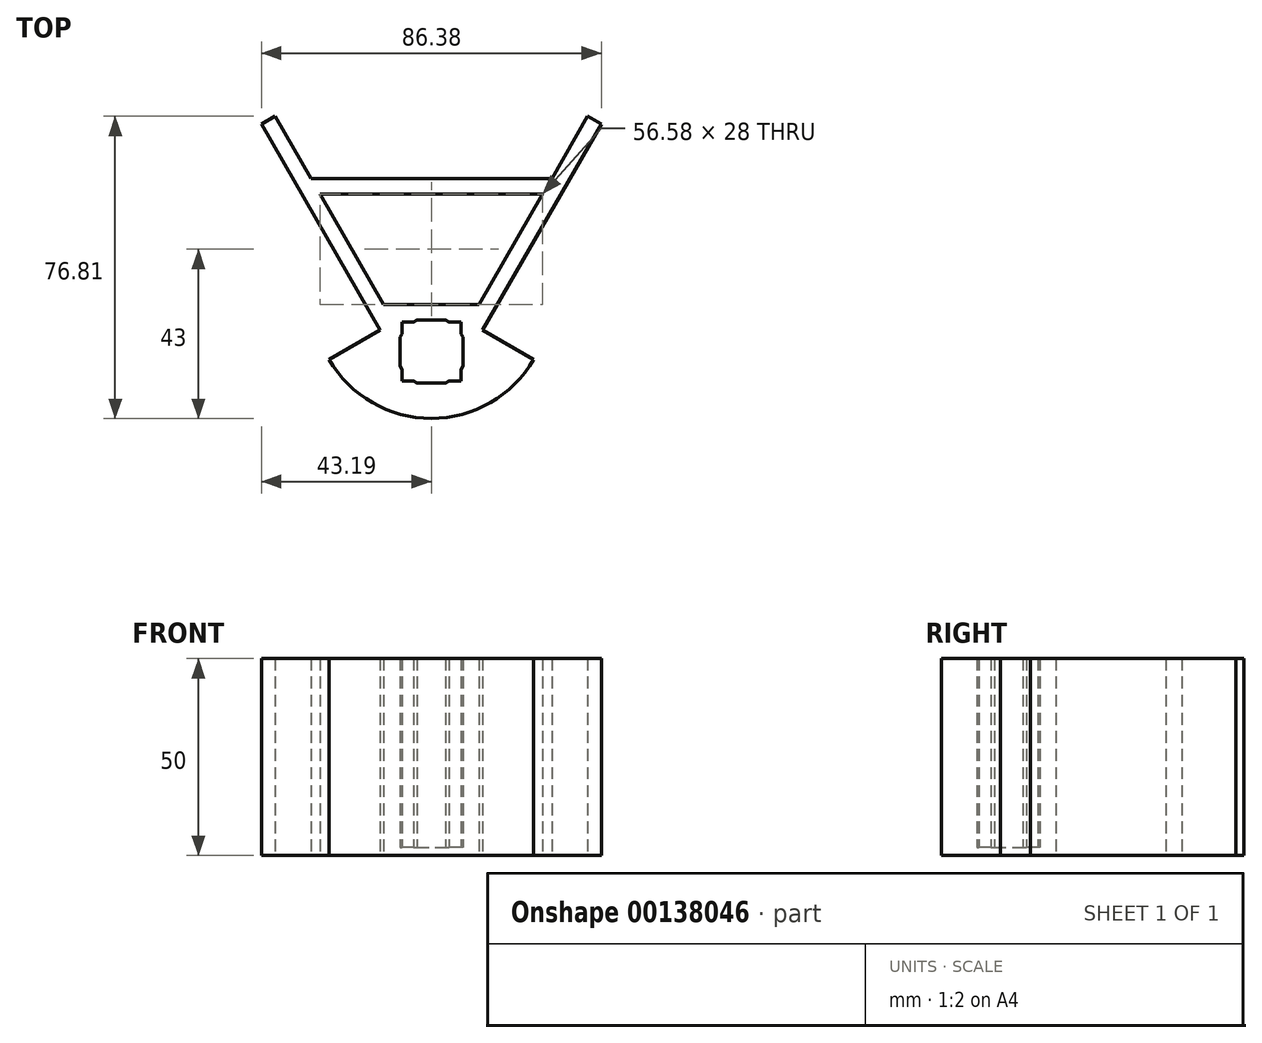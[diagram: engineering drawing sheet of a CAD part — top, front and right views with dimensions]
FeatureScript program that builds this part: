
annotation { "Feature Type Name" : "Feature", "Feature Type Description" : "" }
export const myFeature = defineFeature(function(context is Context, id is Id, definition is map)
    precondition{}
    {
        {
            var Q0;
            Q0=qCreatedBy(makeId("Top.planeOp"),FACE);
            var sketch = newSketch(context, id + "F0", { "sketchPlane" : qUnion([Q0])});
            skLineSegment(sketch, "E0.bottom", {"start": v(7.5, -7.5) * mm, "end": v(-7.5, -7.5) * mm});
            skLineSegment(sketch, "E0.top", {"start": v(7.5, 7.5) * mm, "end": v(-7.5, 7.5) * mm});
            skLineSegment(sketch, "E0.left", {"start": v(7.5, -7.5) * mm, "end": v(7.5, 7.5) * mm});
            skLineSegment(sketch, "E0.right", {"start": v(-7.5, -7.5) * mm, "end": v(-7.5, 7.5) * mm});
            skPoint(sketch, "E0.middle", {"position": v(0, 0) * mm});
            skLineSegment(sketch, "E1", {"start": v(-43.2, 57.8) * mm, "end": v(-13, 5.5) * mm});
            skLineSegment(sketch, "E2", {"start": v(-13, 5.5) * mm, "end": v(-25.98, -2) * mm});
            skLineSegment(sketch, "E3", {"start": v(-43.2, 57.8) * mm, "end": v(-39.73, 59.8) * mm});
            skLineSegment(sketch, "E4", {"start": v(-39.73, 59.8) * mm, "end": v(-30.6, 44) * mm});
            skLineSegment(sketch, "E5", {"start": v(-30.6, 44) * mm, "end": v(0, 44) * mm});
            skArc(sketch, "E6", {"start": v(-25.98, -2) * mm, "mid": v(-15, -12.98) * mm, "end": v(0, -17) * mm});
            skPoint(sketch, "E7", {"position": v(0, 7.5) * mm});
            skLineSegment(sketch, "E8", {"start": v(-25.98, -2) * mm, "end": v(0, -47) * mm, "construction": true});
            skLineSegment(sketch, "E9.MirrorCS", {"start": v(30.6, 44) * mm, "end": v(0, 44) * mm});
            skLineSegment(sketch, "E10.MirrorCS", {"start": v(39.73, 59.8) * mm, "end": v(30.6, 44) * mm});
            skLineSegment(sketch, "E11.MirrorCS", {"start": v(43.2, 57.8) * mm, "end": v(39.73, 59.8) * mm});
            skLineSegment(sketch, "E12.MirrorCS", {"start": v(43.2, 57.8) * mm, "end": v(13, 5.5) * mm});
            skLineSegment(sketch, "E13.MirrorCS", {"start": v(13, 5.5) * mm, "end": v(25.98, -2) * mm});
            skArc(sketch, "E14.MirrorCS", {"start": v(25.98, -2) * mm, "mid": v(15, -12.98) * mm, "end": v(0, -17) * mm});
            skLineSegment(sketch, "E15", {"start": v(-13, 5.5) * mm, "end": v(0, -17) * mm, "construction": true});
            skLineSegment(sketch, "E16", {"start": v(28.3, 40) * mm, "end": v(12.12, 12) * mm});
            skLineSegment(sketch, "E17", {"start": v(12.12, 12) * mm, "end": v(-12.12, 12) * mm});
            skLineSegment(sketch, "E18", {"start": v(-12.12, 12) * mm, "end": v(-28.3, 40) * mm});
            skLineSegment(sketch, "E19", {"start": v(-28.3, 40) * mm, "end": v(28.3, 40) * mm});
            skLineSegment(sketch, "E20", {"start": v(-28.3, 40) * mm, "end": v(-30.6, 44) * mm, "construction": true});
            skLineSegment(sketch, "E21", {"start": v(28.3, 40) * mm, "end": v(30.6, 44) * mm, "construction": true});
            skSolve(sketch);
        }
        {
            var Q0;
            Q0 = qSketchRegion(id + "F0", true);
            extrude(context, id + "F1", {"entities" : qUnion([Q0]), "depth" : 50 * mm});
        }
        {
            var Q0;
            Q0=qCreatedBy(makeId("Top.planeOp"),FACE);
            var sketch = newSketch(context, id + "F2", { "sketchPlane" : qUnion([Q0])});
            skLineSegment(sketch, "E22.bottom", {"start": v(7.5, 7.5) * mm, "end": v(-7.5, 7.5) * mm});
            skLineSegment(sketch, "E22.top", {"start": v(7.5, -7.5) * mm, "end": v(-7.5, -7.5) * mm});
            skLineSegment(sketch, "E22.left", {"start": v(7.5, 7.5) * mm, "end": v(7.5, -7.5) * mm});
            skLineSegment(sketch, "E22.right", {"start": v(-7.5, 7.5) * mm, "end": v(-7.5, -7.5) * mm});
            skSolve(sketch);
        }
        {
            var Q0;
            Q0 = qSketchRegion(id + "F2", true);
            extrude(context, id + "F3", {"entities" : qUnion([Q0]), "operationType" : NewBodyOperationType.ADD, "depth" : 2 * mm});
        }
        {
            var Q0;
            Q0=makeQuery(id+"F3.opExtrude","CAP_FACE",FACE,{"disambiguationData":[OSD([sQuery(id+"F2.wireOp",EDGE,"E22.bottom"),sQuery(id+"F2.wireOp",EDGE,"E22.top"),sQuery(id+"F2.wireOp",EDGE,"E22.left"),sQuery(id+"F2.wireOp",EDGE,"E22.right")])],"isStart":false});
            var sketch = newSketch(context, id + "F4", { "sketchPlane" : qUnion([Q0])});
            skLineSegment(sketch, "E23", {"start": v(7.5, -4.5) * mm, "end": v(7.5, 4.5) * mm});
            skLineSegment(sketch, "E24", {"start": v(7.5, 4.5) * mm, "end": v(8, 3.63) * mm});
            skLineSegment(sketch, "E25", {"start": v(8, 3.63) * mm, "end": v(8, -3.63) * mm});
            skLineSegment(sketch, "E26", {"start": v(8, -3.63) * mm, "end": v(7.5, -4.5) * mm});
            skLineSegment(sketch, "E27", {"start": v(8, 0) * mm, "end": v(7.5, 0) * mm, "construction": true});
            skLineSegment(sketch, "E28", {"start": v(7.5, 0) * mm, "end": v(0, 0) * mm, "construction": true});
            skLineSegment(sketch, "E29.1.0", {"start": v(4.5, 7.5) * mm, "end": v(-4.5, 7.5) * mm});
            skLineSegment(sketch, "E29.1.1", {"start": v(3.63, 8) * mm, "end": v(4.5, 7.5) * mm});
            skLineSegment(sketch, "E29.1.2", {"start": v(-3.63, 8) * mm, "end": v(3.63, 8) * mm});
            skLineSegment(sketch, "E29.1.3", {"start": v(-4.5, 7.5) * mm, "end": v(-3.63, 8) * mm});
            skLineSegment(sketch, "E29.2.0", {"start": v(-7.5, 4.5) * mm, "end": v(-7.5, -4.5) * mm});
            skLineSegment(sketch, "E29.2.1", {"start": v(-8, 3.63) * mm, "end": v(-7.5, 4.5) * mm});
            skLineSegment(sketch, "E29.2.2", {"start": v(-8, -3.63) * mm, "end": v(-8, 3.63) * mm});
            skLineSegment(sketch, "E29.2.3", {"start": v(-7.5, -4.5) * mm, "end": v(-8, -3.63) * mm});
            skLineSegment(sketch, "E29.3.0", {"start": v(-4.5, -7.5) * mm, "end": v(4.5, -7.5) * mm});
            skLineSegment(sketch, "E29.3.1", {"start": v(-3.63, -8) * mm, "end": v(-4.5, -7.5) * mm});
            skLineSegment(sketch, "E29.3.2", {"start": v(3.63, -8) * mm, "end": v(-3.63, -8) * mm});
            skLineSegment(sketch, "E29.3.3", {"start": v(4.5, -7.5) * mm, "end": v(3.63, -8) * mm});
            skPoint(sketch, "E29.center", {"position": v(0, 0) * mm});
            skSolve(sketch);
        }
        {
            var Q0;
            Q0 = qSketchRegion(id + "F4", true);
            extrude(context, id + "F5", {"entities" : qUnion([Q0]), "operationType" : NewBodyOperationType.REMOVE, "endBound" : BoundingType.THROUGH_ALL, "depth" : 25 * mm});
        }
    });
